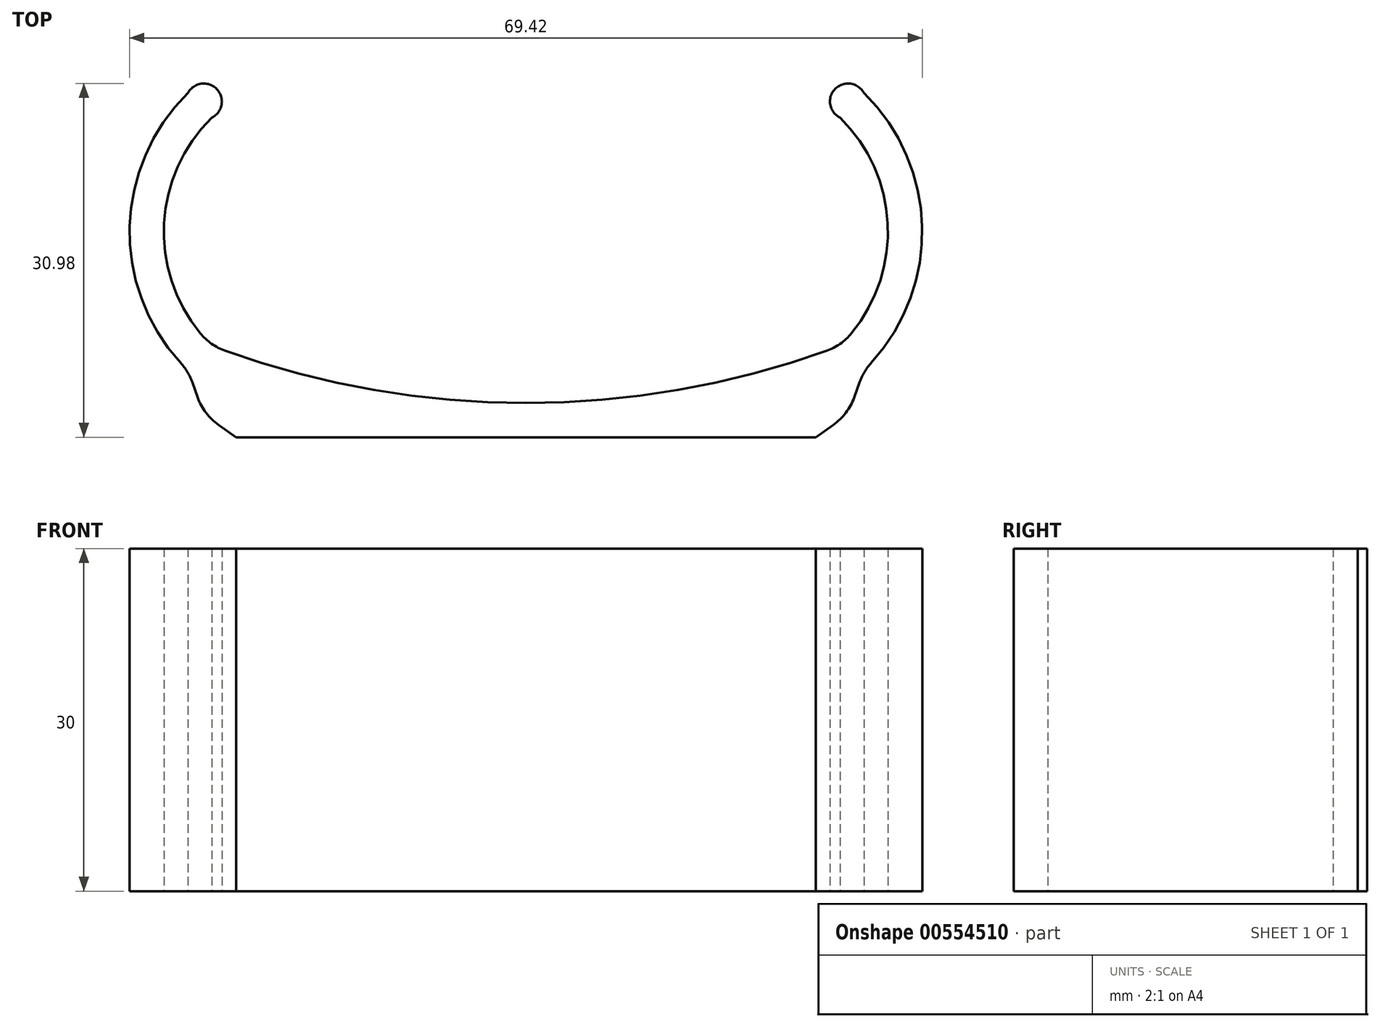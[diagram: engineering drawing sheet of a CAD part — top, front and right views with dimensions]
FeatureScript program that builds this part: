
annotation { "Feature Type Name" : "Feature", "Feature Type Description" : "" }
export const myFeature = defineFeature(function(context is Context, id is Id, definition is map)
    precondition{}
    {
        {
            var Q0;
            Q0=qCreatedBy(makeId("Top.planeOp"),FACE);
            var sketch = newSketch(context, id + "F0", { "sketchPlane" : qUnion([Q0])});
            skLineSegment(sketch, "E0", {"start": v(-27.5, 0) * mm, "end": v(27.5, 0) * mm});
            skArc(sketch, "E1.MirrorCS", {"start": v(26.34, 7.57) * mm, "mid": v(0, 3) * mm, "end": v(-26.34, 7.57) * mm});
            skPoint(sketch, "E2", {"position": v(13.75, 0) * mm});
            skPoint(sketch, "E3", {"position": v(0, 33) * mm});
            skPoint(sketch, "E4", {"position": v(27.5, 28) * mm});
            skPoint(sketch, "E5", {"position": v(-27.5, 28) * mm});
            skPoint(sketch, "E6", {"position": v(27.5, 18) * mm});
            skArc(sketch, "E7", {"start": v(28.5, 9.1) * mm, "mid": v(31.69, 18.75) * mm, "end": v(27.5, 28) * mm});
            skPoint(sketch, "E7.third.point", {"position": v(3.73, 18) * mm});
            skArc(sketch, "E8.MirrorCS", {"start": v(-28.5, 9.1) * mm, "mid": v(-31.69, 18.75) * mm, "end": v(-27.5, 28) * mm});
            skArc(sketch, "E9.0", {"start": v(-30.25, 6.53) * mm, "mid": v(-34.7, 18.47) * mm, "end": v(-29.6, 30.14) * mm});
            skLineSegment(sketch, "E10", {"start": v(-29.24, 4.85) * mm, "end": v(-27.5, 0) * mm});
            skArc(sketch, "E11.MirrorCS", {"start": v(30.25, 6.53) * mm, "mid": v(34.7, 18.47) * mm, "end": v(29.6, 30.14) * mm});
            skLineSegment(sketch, "E12.MirrorCS", {"start": v(29.24, 4.85) * mm, "end": v(27.5, 0) * mm});
            skArc(sketch, "E13", {"start": v(-27.5, 28) * mm, "mid": v(-27.08, 30.5) * mm, "end": v(-29.6, 30.14) * mm});
            skArc(sketch, "E14.MirrorCS", {"start": v(27.5, 28) * mm, "mid": v(27.08, 30.5) * mm, "end": v(29.6, 30.14) * mm});
            skPoint(sketch, "E15.newPointA", {"position": v(-27.5, 8) * mm});
            skPoint(sketch, "E15.newPointB", {"position": v(-27.5, 8) * mm});
            skArc(sketch, "E15.filletArc", {"start": v(-28.5, 9.1) * mm, "mid": v(-27.53, 8.19) * mm, "end": v(-26.34, 7.57) * mm});
            skPoint(sketch, "E16.visualSharp", {"position": v(27.5, 8) * mm});
            skArc(sketch, "E16.filletArc", {"start": v(26.34, 7.57) * mm, "mid": v(27.53, 8.19) * mm, "end": v(28.5, 9.1) * mm});
            skPoint(sketch, "E17.visualSharp", {"position": v(29.6, 5.86) * mm});
            skArc(sketch, "E17.filletArc", {"start": v(30.25, 6.53) * mm, "mid": v(29.66, 5.74) * mm, "end": v(29.24, 4.85) * mm});
            skPoint(sketch, "E18.visualSharp", {"position": v(-29.6, 5.86) * mm});
            skArc(sketch, "E18.filletArc", {"start": v(-29.24, 4.85) * mm, "mid": v(-29.66, 5.74) * mm, "end": v(-30.25, 6.53) * mm});
            skSolve(sketch);
        }
        {
            var Q0;
            Q0 = qSketchRegion(id + "F0", true);
            extrude(context, id + "F1", {"entities" : qUnion([Q0]), "depth" : 30 * mm, "offsetDistance" : 25 * mm});
        }
        {
            var Q0;
            Q0=makeQuery(id+"F1.opExtrude","SWEPT_EDGE",EDGE,{"disambiguationData":[OSD([sQuery(id+"F0.wireOp",EDGE,"E0"),sQuery(id+"F0.wireOp",EDGE,"E10")])]});
            var Q1;
            Q1=makeQuery(id+"F1.opExtrude","SWEPT_EDGE",EDGE,{"disambiguationData":[OSD([sQuery(id+"F0.wireOp",EDGE,"E0"),sQuery(id+"F0.wireOp",EDGE,"E12.MirrorCS")])]});
            chamfer(context, id + "F2", {"entities" : qUnion([Q0, Q1]), "width" : 3 * mm, "tangentPropagation" : true});
        }
        {
            var Q0;
            {var subQ0=sQuery(id+"F0.wireOp",EDGE,"E10");Q0=makeQuery(id+"F2.opChamfer","BLEND_EDGE",EDGE,{"blendedFrom":[makeQuery(id+"F1.opExtrude","SWEPT_EDGE",EDGE,{"disambiguationData":[OSD([sQuery(id+"F0.wireOp",EDGE,"E0"),subQ0])]}),makeQuery(id+"F1.opExtrude","SWEPT_FACE",FACE,{"disambiguationData":[OSD([subQ0])]})],"blendedInto":[makeQuery(id+"F1.opExtrude","SWEPT_FACE",FACE,{"disambiguationData":[OSD([subQ0])]})]});}
            var Q1;
            {var subQ0=sQuery(id+"F0.wireOp",EDGE,"E12.MirrorCS");Q1=makeQuery(id+"F2.opChamfer","BLEND_EDGE",EDGE,{"blendedFrom":[makeQuery(id+"F1.opExtrude","SWEPT_EDGE",EDGE,{"disambiguationData":[OSD([sQuery(id+"F0.wireOp",EDGE,"E0"),subQ0])]}),makeQuery(id+"F1.opExtrude","SWEPT_FACE",FACE,{"disambiguationData":[OSD([subQ0])]})],"blendedInto":[makeQuery(id+"F1.opExtrude","SWEPT_FACE",FACE,{"disambiguationData":[OSD([subQ0])]})]});}
            fillet(context, id + "F3", {"entities" : qUnion([Q0, Q1]), "radius" : 5 * mm, "tangentPropagation" : true, "allowEdgeOverflow" : false});
        }
    });
